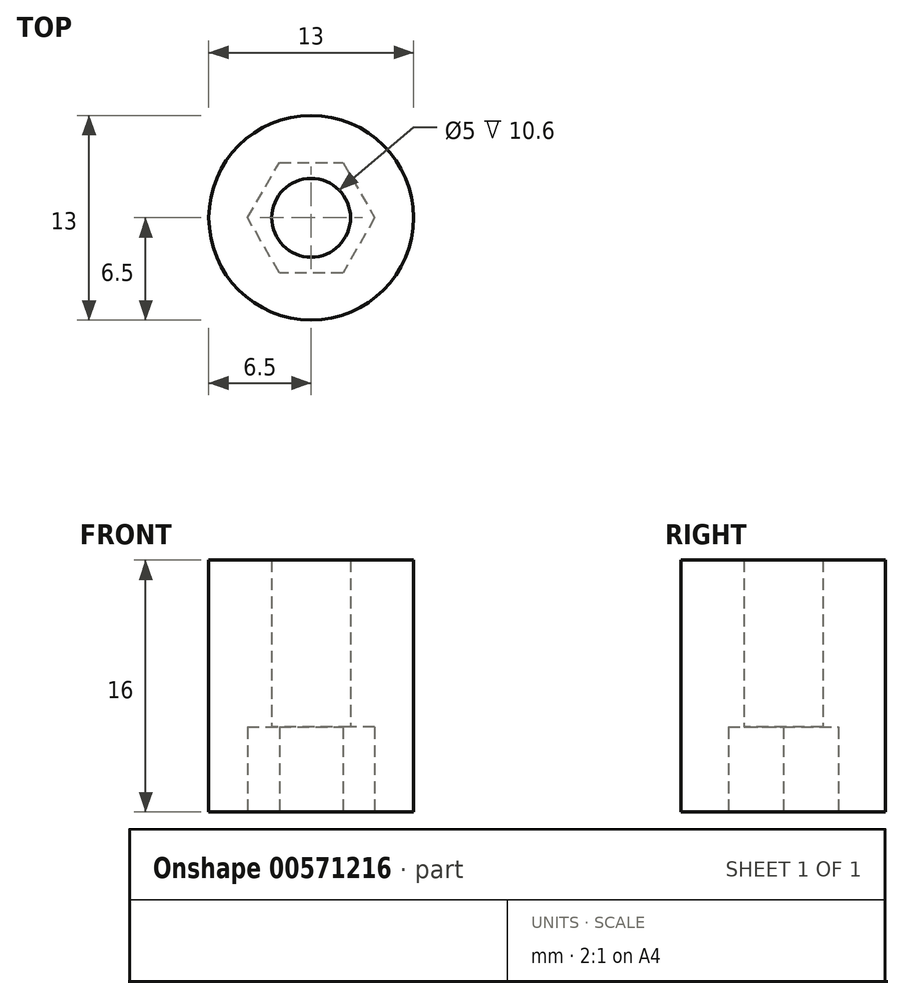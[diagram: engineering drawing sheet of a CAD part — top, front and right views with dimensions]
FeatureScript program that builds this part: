
annotation { "Feature Type Name" : "Feature", "Feature Type Description" : "" }
export const myFeature = defineFeature(function(context is Context, id is Id, definition is map)
    precondition{}
    {
        {
            var Q0;
            Q0=qCreatedBy(makeId("Top.planeOp"),FACE);
            var sketch = newSketch(context, id + "F0", { "sketchPlane" : qUnion([Q0])});
            skCircle(sketch, "E0", {"center": v(0, 0) * mm, "radius": 6.5 * mm});
            skCircle(sketch, "E1", {"center": v(0, 0) * mm, "radius": 2.5 * mm});
            skCircle(sketch, "E2.cCircle", {"center": v(0, 0) * mm, "radius": 3.5 * mm, "construction": true});
            skLineSegment(sketch, "E2.0", {"start": v(-2.02, 3.5) * mm, "end": v(2.02, 3.5) * mm});
            skLineSegment(sketch, "E2.1", {"start": v(2.02, 3.5) * mm, "end": v(4.04, 0) * mm});
            skLineSegment(sketch, "E2.2", {"start": v(4.04, 0) * mm, "end": v(2.02, -3.5) * mm});
            skLineSegment(sketch, "E2.3", {"start": v(2.02, -3.5) * mm, "end": v(-2.02, -3.5) * mm});
            skLineSegment(sketch, "E2.4", {"start": v(-2.02, -3.5) * mm, "end": v(-4.04, 0) * mm});
            skLineSegment(sketch, "E2.5", {"start": v(-4.04, 0) * mm, "end": v(-2.02, 3.5) * mm});
            skPoint(sketch, "E2.0.midPoint", {"position": v(0, 3.5) * mm});
            skSolve(sketch);
        }
        {
            var Q0;
            Q0=makeQuery(id+"F0.imprint","IMPRINT",FACE,{"disambiguationData":[TD([[makeQuery(id+"F0.imprint","IMPRINT",EDGE,{"derivedFrom":sQuery(id+"F0.wireOp",EDGE,"E0")}),1.0]])]});
            var Q1;
            Q1=makeQuery(id+"F0.imprint","IMPRINT",FACE,{"disambiguationData":[TD([[makeQuery(id+"F0.imprint","IMPRINT",EDGE,{"derivedFrom":sQuery(id+"F0.wireOp",EDGE,"E1")}),-1.0]])]});
            extrude(context, id + "F1", {"entities" : qUnion([Q0, Q1]), "depth" : 16 * mm, "offsetDistance" : 25 * mm});
        }
        {
            var Q0;
            Q0=makeQuery(id+"F0.imprint","IMPRINT",FACE,{"disambiguationData":[TD([[makeQuery(id+"F0.imprint","IMPRINT",EDGE,{"derivedFrom":sQuery(id+"F0.wireOp",EDGE,"E1")}),-1.0]])]});
            extrude(context, id + "F2", {"entities" : qUnion([Q0]), "operationType" : NewBodyOperationType.REMOVE, "depth" : 5.4 * mm, "offsetDistance" : 25 * mm});
        }
    });
